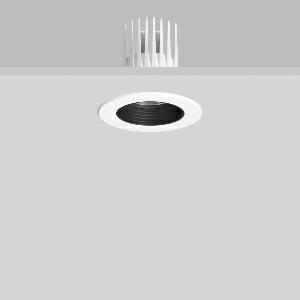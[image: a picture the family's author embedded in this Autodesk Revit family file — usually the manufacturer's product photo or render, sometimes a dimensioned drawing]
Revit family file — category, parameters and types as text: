
# Revit family: heledon_mini_e_901743_002_2_76_5112
name_source: partatom
category: Lighting Fixtures
units: mm (PartAtom-declared; Revit-internal decimal feet)

## family parameters
Cut with Voids When Loaded = No
Host = Face
Light Source = No
Part Type = Normal
Room Calculation Point = No
Round Connector Dimension = Use Diameter
Shared = No

## types (1)
- HELEDON mini E (1 x LED Modul 927, 2100 lm, 2700)
    Apparent Load = 20 VA
    Approval mark = CE
    CIE Flux Codes = 99 100 100 100 100
    Color Rendering = 92
    Color Temperature = 2700
    Default Elevation = 1800 mm
    Description = Series: HELEDON mini
Round recessed downlight. Housing: die-cast aluminium, powder-coated. Black plastic ring and recessed LED to prevent glare from the side. Optical assembly with lens made of plastic (polycarbonate) for the best homogeneous light distribution - can be changed without tools. Best colour rendering index Ra>90. Suitable for Recessed ceiling mounting. Installation without tools thanks to spring fastening system. Including separate LED converter with connecting cable 600 mm.High quality converter without flickering and stroboscopic effect. Through-wiring box (5 pole) available as accessory. The following accessories can be mounted without use of tools: interchangeable lenses, decorative glasses, honeycomb louvre, clear and frosted diffusers, white interchangeable plastic ring. 
Colour: traffic white, matt (RAL 9016)
Diameter: 124 mm
Height: 3 mm
Cut-out diameter: 114 mm
Recess height: 170 mm
Luminaire: recess height: 120 mm
Lamp: LED
Socket: without socket
Colour temperature: 2700K
Colour rendering index (CRI): 92
System power: 20 W
Rated luminous flux: 2100 lm
Luminous efficiency: 105 lm/W
Control gear: Converter, dimmable, DALI
Protection class: II
Type of protection: IP 20
    Height = 0 mm  [stored 0 ft]
    Lamp = 1 x LED Modul 927
    Lamp Light Flux = 2100 lm
    Lamp count = 1
    Length = 124 mm
    Lifetime = 50000 h
    Luminous efficacy = 105 lm/W
    Manufacturer = RZB
    ModVariant = No
    Model = 901743.002.2.76
    Mounting Place = Ceiling
    Mounting Type = Recessed
    Number of Poles = 1
    OnlyDefault = Yes
    Power Factor = 1
    Product Name = HELEDON mini E
    Product group = Recessed downlights
    ProductGroupID = 402
    Protection Class = Protection class II
    Protection Degree = IP 20
    RLX_Detail_Level = 1
    RLX_Emergency_Light_Flux = 0 lm
    RLX_Emergency_Type = 0
    RLX_Emergency_Type_DB = No
    RlxData = <blob elided: 123121 chars, md5=f41fb3a7>
    Socket = socket
    Standby Power = 0 W
    System Light Flux = 2100 lm
    System Power = 20 W
    Type Comments = Product without accessories
    Type Image = 901656.002.jpg
    URL = http://relux.com
    VarID = ---
    Voltage = 230 V
    Voltage Range = 220-240 V
    Weight = 0.00 kg
    Width = 0 mm  [stored 0 ft]

note: [stored X ft] marks values corroborated as IEEE doubles in the binary element streams (Revit-internal decimal feet)

## geometry (parser evidence)
native form markers: Blend x4, Sweep x11
no freeform markers — native parametric forms only
